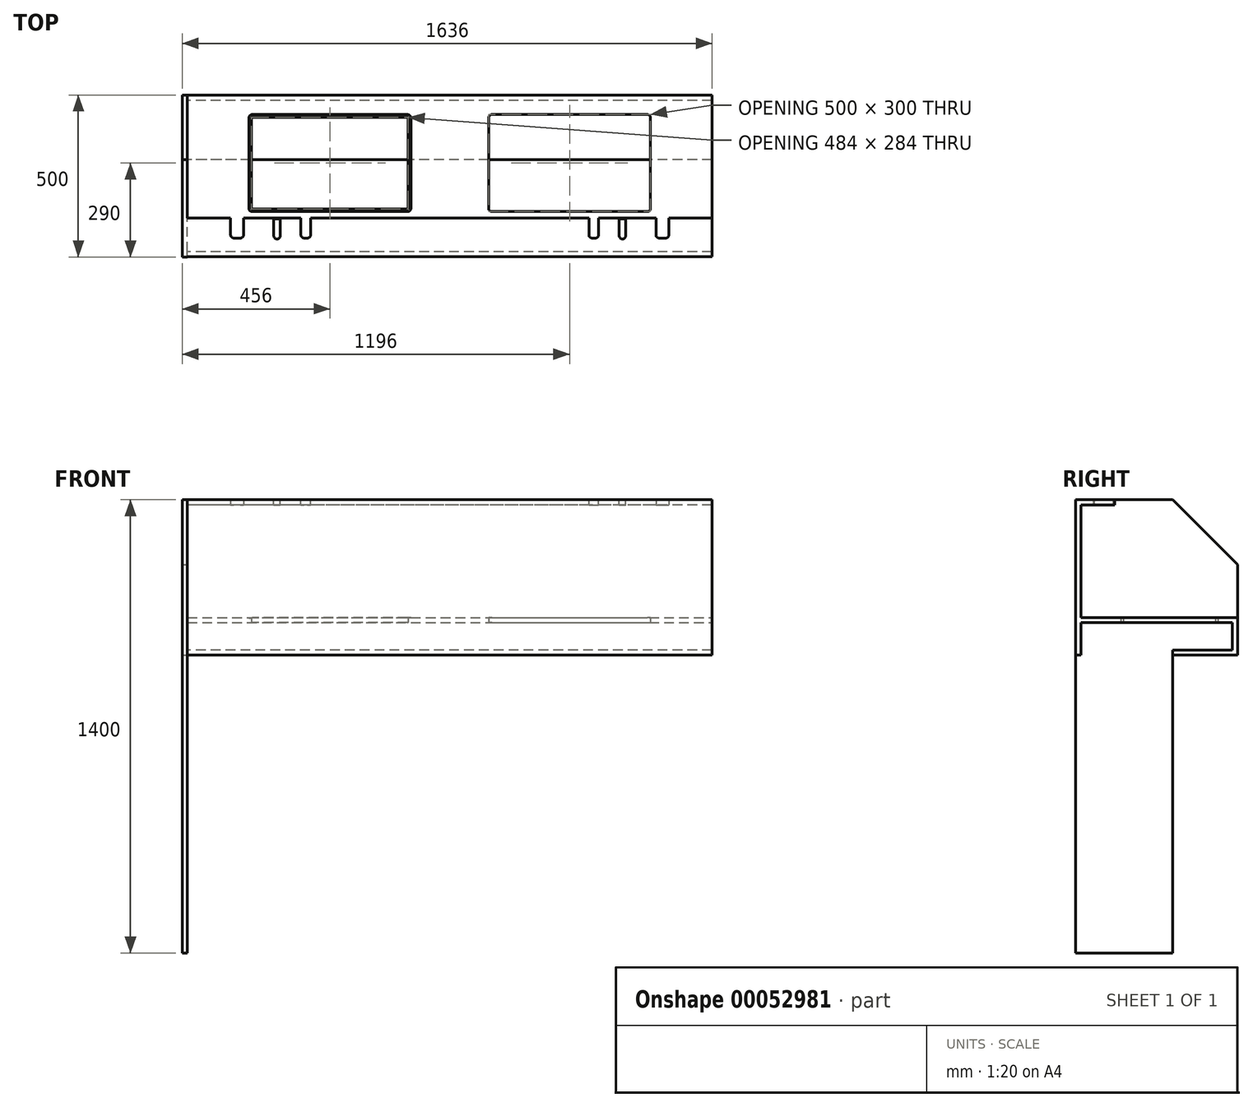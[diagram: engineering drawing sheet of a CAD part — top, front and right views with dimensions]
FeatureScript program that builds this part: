
annotation { "Feature Type Name" : "Feature", "Feature Type Description" : "" }
export const myFeature = defineFeature(function(context is Context, id is Id, definition is map)
    precondition{}
    {
        {
            var Q0;
            Q0=qCreatedBy(makeId("Right.planeOp"),FACE);
            var sketch = newSketch(context, id + "F0", { "sketchPlane" : qUnion([Q0])});
            skLineSegment(sketch, "E0", {"start": v(-300, 480) * mm, "end": v(-300, -920) * mm});
            skLineSegment(sketch, "E1", {"start": v(0, -920) * mm, "end": v(-300, -920) * mm});
            skLineSegment(sketch, "E2", {"start": v(200, 0) * mm, "end": v(200, 280) * mm});
            skLineSegment(sketch, "E3", {"start": v(200, 280) * mm, "end": v(0, 480) * mm});
            skLineSegment(sketch, "E4", {"start": v(0, 480) * mm, "end": v(-300, 480) * mm});
            skLineSegment(sketch, "E5", {"start": v(0, 647.9) * mm, "end": v(0, -1632.93) * mm, "construction": true});
            skLineSegment(sketch, "E6", {"start": v(-901.91, 0) * mm, "end": v(413.04, 0) * mm, "construction": true});
            skLineSegment(sketch, "E7", {"start": v(0, -920) * mm, "end": v(0, 0) * mm});
            skLineSegment(sketch, "E8", {"start": v(0, 0) * mm, "end": v(200, 0) * mm});
            skPoint(sketch, "E9.orphan", {"position": v(1728, 0) * mm});
            skSolve(sketch);
        }
        {
            var Q0;
            Q0=makeQuery(id+"F0.imprint","IMPRINT",FACE,{"disambiguationData":[TD([[makeQuery(id+"F0.imprint","IMPRINT",EDGE,{"derivedFrom":sQuery(id+"F0.wireOp",EDGE,"E0")}),1.0]])]});
            var Q1;
            Q1 = qSketchRegion(id + "F3", true);
            extrude(context, id + "F1", {"entities" : qUnion([Q0, Q1]), "oppositeDirection" : true, "depth" : 16 * mm});
        }
        {
            var Q0;
            Q0=qCreatedBy(makeId("Top.planeOp"),FACE);
            cPlane(context, id + "F2", {"entities" : qUnion([Q0]), "cplaneType" : CPlaneType.OFFSET, "offset" : 100 * mm, "width" : 150 * mm, "height" : 150 * mm});
        }
        {
            var Q0;
            Q0=qCreatedBy(id+"F2.planeOp",FACE);
            var sketch = newSketch(context, id + "F3", { "sketchPlane" : qUnion([Q0])});
            skLineSegment(sketch, "E10.bottom", {"start": v(0, -284) * mm, "end": v(1620, -284) * mm});
            skLineSegment(sketch, "E10.top", {"start": v(0, 200) * mm, "end": v(1620, 200) * mm});
            skLineSegment(sketch, "E10.left", {"start": v(0, -284) * mm, "end": v(0, 200) * mm});
            skLineSegment(sketch, "E10.right", {"start": v(1620, -284) * mm, "end": v(1620, 200) * mm});
            skLineSegment(sketch, "E11", {"start": v(0, 0) * mm, "end": v(1326.37, 0) * mm, "construction": true});
            skLineSegment(sketch, "E12", {"start": v(810, -795.49) * mm, "end": v(810, 1180.36) * mm, "construction": true});
            skPoint(sketch, "E12.endSnap0", {"position": v(810, 200) * mm});
            skLineSegment(sketch, "E13.top", {"start": v(680, 140) * mm, "end": v(200, 140) * mm});
            skLineSegment(sketch, "E13.left", {"start": v(690, -150) * mm, "end": v(690, 130) * mm});
            skLineSegment(sketch, "E13.right", {"start": v(190, -150) * mm, "end": v(190, 130) * mm});
            skLineSegment(sketch, "E14", {"start": v(680, -160) * mm, "end": v(200, -160) * mm});
            skPoint(sketch, "E15.visualSharp", {"position": v(690, -160) * mm});
            skArc(sketch, "E15.filletArc", {"start": v(680, -160) * mm, "mid": v(687.07, -157.07) * mm, "end": v(690, -150) * mm});
            skPoint(sketch, "E16.visualSharp", {"position": v(190, -160) * mm});
            skArc(sketch, "E16.filletArc", {"start": v(190, -150) * mm, "mid": v(192.93, -157.07) * mm, "end": v(200, -160) * mm});
            skPoint(sketch, "E17.visualSharp", {"position": v(190, 140) * mm});
            skArc(sketch, "E17.filletArc", {"start": v(200, 140) * mm, "mid": v(192.93, 137.07) * mm, "end": v(190, 130) * mm});
            skPoint(sketch, "E18.visualSharp", {"position": v(690, 140) * mm});
            skArc(sketch, "E18.filletArc", {"start": v(690, 130) * mm, "mid": v(687.07, 137.07) * mm, "end": v(680, 140) * mm});
            skArc(sketch, "E19.0", {"start": v(680, -152) * mm, "mid": v(681.41, -151.41) * mm, "end": v(682, -150) * mm});
            skLineSegment(sketch, "E19.1", {"start": v(682, -150) * mm, "end": v(682, 130) * mm});
            skLineSegment(sketch, "E19.2", {"start": v(680, -152) * mm, "end": v(200, -152) * mm});
            skArc(sketch, "E19.3", {"start": v(682, 130) * mm, "mid": v(681.41, 131.41) * mm, "end": v(680, 132) * mm});
            skArc(sketch, "E19.4", {"start": v(198, -150) * mm, "mid": v(198.59, -151.41) * mm, "end": v(200, -152) * mm});
            skLineSegment(sketch, "E19.5", {"start": v(198, -150) * mm, "end": v(198, 130) * mm});
            skArc(sketch, "E19.6", {"start": v(200, 132) * mm, "mid": v(198.59, 131.41) * mm, "end": v(198, 130) * mm});
            skLineSegment(sketch, "E19.7", {"start": v(680, 132) * mm, "end": v(200, 132) * mm});
            skArc(sketch, "E20.MirrorCS", {"start": v(1420, 140) * mm, "mid": v(1427.07, 137.07) * mm, "end": v(1430, 130) * mm});
            skArc(sketch, "E21.MirrorCS", {"start": v(1420, 132) * mm, "mid": v(1421.41, 131.41) * mm, "end": v(1422, 130) * mm});
            skArc(sketch, "E22.MirrorCS", {"start": v(1422, -150) * mm, "mid": v(1421.41, -151.41) * mm, "end": v(1420, -152) * mm});
            skArc(sketch, "E23.MirrorCS", {"start": v(930, 130) * mm, "mid": v(932.93, 137.07) * mm, "end": v(940, 140) * mm});
            skArc(sketch, "E24.MirrorCS", {"start": v(940, -152) * mm, "mid": v(938.59, -151.41) * mm, "end": v(938, -150) * mm});
            skArc(sketch, "E25.MirrorCS", {"start": v(940, -160) * mm, "mid": v(932.93, -157.07) * mm, "end": v(930, -150) * mm});
            skArc(sketch, "E26.MirrorCS", {"start": v(1430, -150) * mm, "mid": v(1427.07, -157.07) * mm, "end": v(1420, -160) * mm});
            skLineSegment(sketch, "E27.MirrorCS", {"start": v(938, -150) * mm, "end": v(938, 130) * mm});
            skLineSegment(sketch, "E28.MirrorCS", {"start": v(1430, -150) * mm, "end": v(1430, 130) * mm});
            skPoint(sketch, "E29.MirrorP", {"position": v(930, 140) * mm});
            skLineSegment(sketch, "E30.MirrorCS", {"start": v(930, -150) * mm, "end": v(930, 130) * mm});
            skLineSegment(sketch, "E31.MirrorCS", {"start": v(940, -152) * mm, "end": v(1420, -152) * mm});
            skLineSegment(sketch, "E32.MirrorCS", {"start": v(940, 140) * mm, "end": v(1420, 140) * mm});
            skPoint(sketch, "E33.MirrorP", {"position": v(1430, 140) * mm});
            skLineSegment(sketch, "E34.MirrorCS", {"start": v(940, 132) * mm, "end": v(1420, 132) * mm});
            skLineSegment(sketch, "E35.MirrorCS", {"start": v(1422, -150) * mm, "end": v(1422, 130) * mm});
            skLineSegment(sketch, "E36.MirrorCS", {"start": v(940, -160) * mm, "end": v(1420, -160) * mm});
            skPoint(sketch, "E37.MirrorP", {"position": v(1430, -160) * mm});
            skPoint(sketch, "E38.MirrorP", {"position": v(930, -160) * mm});
            skSolve(sketch);
        }
        {
            var Q0;
            Q0=makeQuery(id+"F3.imprint","IMPRINT",FACE,{"disambiguationData":[TD([[makeQuery(id+"F3.imprint","IMPRINT",EDGE,{"derivedFrom":sQuery(id+"F3.wireOp",EDGE,"E10.bottom")}),1.0]])]});
            extrude(context, id + "F4", {"entities" : qUnion([Q0]), "operationType" : NewBodyOperationType.ADD, "depth" : 16 * mm});
        }
        {
            var Q0;
            Q0=makeQuery(id+"F3.imprint","IMPRINT",FACE,{"disambiguationData":[TD([[makeQuery(id+"F3.imprint","IMPRINT",EDGE,{"derivedFrom":sQuery(id+"F3.wireOp",EDGE,"E13.top")}),1.0]])]});
            var Q1;
            Q1=makeQuery(id+"F3.imprint","IMPRINT",FACE,{"disambiguationData":[TD([[makeQuery(id+"F3.imprint","IMPRINT",EDGE,{"derivedFrom":sQuery(id+"F3.wireOp",EDGE,"E20.MirrorCS")}),-1.0]])]});
            extrude(context, id + "F5", {"entities" : qUnion([Q0, Q1]), "operationType" : NewBodyOperationType.ADD, "depth" : 14 * mm});
        }
        {
            var Q0;
            Q0=makeQuery(id+"F0.imprint","IMPRINT",FACE,{"disambiguationData":[TD([[makeQuery(id+"F0.imprint","IMPRINT",EDGE,{"derivedFrom":sQuery(id+"F0.wireOp",EDGE,"E0")}),1.0]])]});
            var sketch = newSketch(context, id + "F6", { "sketchPlane" : qUnion([Q0])});
            skLineSegment(sketch, "E39.bottom", {"start": v(0, 0) * mm, "end": v(0, 0) * mm});
            skLineSegment(sketch, "E40.bottom", {"start": v(184, 16) * mm, "end": v(0, 16) * mm});
            skLineSegment(sketch, "E40.top", {"start": v(184, 0) * mm, "end": v(0, 0) * mm});
            skLineSegment(sketch, "E40.left", {"start": v(184, 16) * mm, "end": v(184, 0) * mm});
            skLineSegment(sketch, "E41", {"start": v(0, 16) * mm, "end": v(0, 0) * mm});
            skLineSegment(sketch, "E42.bottom", {"start": v(184, 0) * mm, "end": v(200, 0) * mm});
            skLineSegment(sketch, "E42.top", {"start": v(184, 100) * mm, "end": v(200, 100) * mm});
            skLineSegment(sketch, "E42.left", {"start": v(184, 0) * mm, "end": v(184, 100) * mm});
            skLineSegment(sketch, "E42.right", {"start": v(200, 0) * mm, "end": v(200, 100) * mm});
            skLineSegment(sketch, "E43.bottom", {"start": v(-299.51, 0) * mm, "end": v(-283.51, 0) * mm});
            skLineSegment(sketch, "E43.top", {"start": v(-299.51, 464) * mm, "end": v(-283.51, 464) * mm});
            skLineSegment(sketch, "E43.left", {"start": v(-299.51, 0) * mm, "end": v(-299.51, 464) * mm});
            skLineSegment(sketch, "E43.right", {"start": v(-283.51, 0) * mm, "end": v(-283.51, 464) * mm});
            skLineSegment(sketch, "E44.bottom", {"start": v(-299.51, 464) * mm, "end": v(-179.51, 464) * mm});
            skLineSegment(sketch, "E44.top", {"start": v(-299.51, 480) * mm, "end": v(-179.51, 480) * mm});
            skLineSegment(sketch, "E44.left", {"start": v(-299.51, 464) * mm, "end": v(-299.51, 480) * mm});
            skLineSegment(sketch, "E44.right", {"start": v(-179.51, 464) * mm, "end": v(-179.51, 480) * mm});
            skSolve(sketch);
        }
        {
            var Q0;
            Q0 = qSketchRegion(id + "F6", true);
            extrude(context, id + "F7", {"entities" : qUnion([Q0]), "operationType" : NewBodyOperationType.ADD, "depth" : 1620 * mm});
        }
        {
            var Q0;
            Q0=makeQuery(id+"F7.boolean.opBoolean","MERGE",FACE,{"derivedFrom":[makeQuery(id+"F1.opExtrude","SWEPT_FACE",FACE,{"disambiguationData":[OSD([sQuery(id+"F0.wireOp",EDGE,"E4")])]}),makeQuery(id+"F7.opExtrude","SWEPT_FACE",FACE,{"disambiguationData":[OSD([sQuery(id+"F6.wireOp",EDGE,"E43.top"),sQuery(id+"F6.wireOp",EDGE,"E44.top")])]})]});
            var sketch = newSketch(context, id + "F8", { "sketchPlane" : qUnion([Q0])});
            skLineSegment(sketch, "E45.bottom", {"start": v(276.69, -244.46) * mm, "end": v(276.69, -244.46) * mm});
            skLineSegment(sketch, "E45.top", {"start": v(266.69, -182.58) * mm, "end": v(286.69, -182.58) * mm});
            skLineSegment(sketch, "E45.left", {"start": v(266.69, -234.46) * mm, "end": v(266.69, -182.58) * mm});
            skLineSegment(sketch, "E45.right", {"start": v(286.69, -234.46) * mm, "end": v(286.69, -182.58) * mm});
            skLineSegment(sketch, "E46.bottom", {"start": v(370.4, -241.58) * mm, "end": v(360.4, -241.58) * mm});
            skLineSegment(sketch, "E46.top", {"start": v(380.4, -171.06) * mm, "end": v(350.4, -171.06) * mm});
            skLineSegment(sketch, "E46.left", {"start": v(380.4, -231.58) * mm, "end": v(380.4, -171.06) * mm});
            skLineSegment(sketch, "E46.right", {"start": v(350.4, -231.58) * mm, "end": v(350.4, -171.06) * mm});
            skLineSegment(sketch, "E47.bottom", {"start": v(173.36, -174.4) * mm, "end": v(133.36, -174.4) * mm});
            skLineSegment(sketch, "E47.top", {"start": v(163.36, -241.58) * mm, "end": v(143.36, -241.58) * mm});
            skLineSegment(sketch, "E47.left", {"start": v(173.36, -174.4) * mm, "end": v(173.36, -231.58) * mm});
            skLineSegment(sketch, "E47.right", {"start": v(133.36, -174.4) * mm, "end": v(133.36, -231.58) * mm});
            skPoint(sketch, "E48.visualSharp", {"position": v(133.36, -241.58) * mm});
            skArc(sketch, "E48.filletArc", {"start": v(133.36, -231.58) * mm, "mid": v(136.3, -238.65) * mm, "end": v(143.36, -241.58) * mm});
            skPoint(sketch, "E49.visualSharp", {"position": v(173.36, -241.58) * mm});
            skArc(sketch, "E49.filletArc", {"start": v(163.36, -241.58) * mm, "mid": v(170.44, -238.65) * mm, "end": v(173.36, -231.58) * mm});
            skPoint(sketch, "E50.visualSharp", {"position": v(266.69, -244.46) * mm});
            skArc(sketch, "E50.filletArc", {"start": v(266.69, -234.46) * mm, "mid": v(269.62, -241.53) * mm, "end": v(276.69, -244.46) * mm});
            skPoint(sketch, "E51.visualSharp", {"position": v(286.69, -244.46) * mm});
            skArc(sketch, "E51.filletArc", {"start": v(276.69, -244.46) * mm, "mid": v(283.76, -241.53) * mm, "end": v(286.69, -234.46) * mm});
            skPoint(sketch, "E52.visualSharp", {"position": v(350.4, -241.58) * mm});
            skArc(sketch, "E52.filletArc", {"start": v(350.4, -231.58) * mm, "mid": v(353.33, -238.65) * mm, "end": v(360.4, -241.58) * mm});
            skPoint(sketch, "E53.visualSharp", {"position": v(380.4, -241.58) * mm});
            skArc(sketch, "E53.filletArc", {"start": v(370.4, -241.58) * mm, "mid": v(377.47, -238.65) * mm, "end": v(380.4, -231.58) * mm});
            skLineSegment(sketch, "E54.MirrorCS", {"start": v(1249.6, -241.58) * mm, "end": v(1259.6, -241.58) * mm});
            skArc(sketch, "E55.MirrorCS", {"start": v(1353.31, -234.46) * mm, "mid": v(1350.38, -241.53) * mm, "end": v(1343.31, -244.46) * mm});
            skArc(sketch, "E56.MirrorCS", {"start": v(1343.31, -244.46) * mm, "mid": v(1336.24, -241.53) * mm, "end": v(1333.31, -234.46) * mm});
            skArc(sketch, "E57.MirrorCS", {"start": v(1269.6, -231.58) * mm, "mid": v(1266.67, -238.65) * mm, "end": v(1259.6, -241.58) * mm});
            skArc(sketch, "E58.MirrorCS", {"start": v(1456.64, -241.58) * mm, "mid": v(1449.56, -238.65) * mm, "end": v(1446.64, -231.58) * mm});
            skArc(sketch, "E59.MirrorCS", {"start": v(1249.6, -241.58) * mm, "mid": v(1242.53, -238.65) * mm, "end": v(1239.6, -231.58) * mm});
            skLineSegment(sketch, "E60.MirrorCS", {"start": v(1456.64, -241.58) * mm, "end": v(1476.64, -241.58) * mm});
            skPoint(sketch, "E61.MirrorP", {"position": v(1353.31, -244.46) * mm});
            skPoint(sketch, "E62.MirrorP", {"position": v(1269.6, -241.58) * mm});
            skPoint(sketch, "E63.MirrorP", {"position": v(1446.64, -241.58) * mm});
            skPoint(sketch, "E64.MirrorP", {"position": v(1239.6, -241.58) * mm});
            skPoint(sketch, "E65.MirrorP", {"position": v(1333.31, -244.46) * mm});
            skLineSegment(sketch, "E66.MirrorCS", {"start": v(1343.31, -244.46) * mm, "end": v(1343.31, -244.46) * mm});
            skLineSegment(sketch, "E67.MirrorCS", {"start": v(1353.31, -182.58) * mm, "end": v(1333.31, -182.58) * mm});
            skLineSegment(sketch, "E68.MirrorCS", {"start": v(1486.64, -174.4) * mm, "end": v(1486.64, -231.58) * mm});
            skLineSegment(sketch, "E69.MirrorCS", {"start": v(1353.31, -234.46) * mm, "end": v(1353.31, -182.58) * mm});
            skLineSegment(sketch, "E70.MirrorCS", {"start": v(1333.31, -234.46) * mm, "end": v(1333.31, -182.58) * mm});
            skLineSegment(sketch, "E71.MirrorCS", {"start": v(1239.6, -171.06) * mm, "end": v(1269.6, -171.06) * mm});
            skLineSegment(sketch, "E72.MirrorCS", {"start": v(1239.6, -231.58) * mm, "end": v(1239.6, -171.06) * mm});
            skLineSegment(sketch, "E73.MirrorCS", {"start": v(1446.64, -174.4) * mm, "end": v(1446.64, -231.58) * mm});
            skLineSegment(sketch, "E74.MirrorCS", {"start": v(1269.6, -231.58) * mm, "end": v(1269.6, -171.06) * mm});
            skLineSegment(sketch, "E75.MirrorCS", {"start": v(1446.64, -174.4) * mm, "end": v(1486.64, -174.4) * mm});
            skArc(sketch, "E76.MirrorCS", {"start": v(1486.64, -231.58) * mm, "mid": v(1483.7, -238.65) * mm, "end": v(1476.64, -241.58) * mm});
            skSolve(sketch);
        }
        {
            var Q0;
            Q0 = qSketchRegion(id + "F8", true);
            extrude(context, id + "F9", {"entities" : qUnion([Q0]), "operationType" : NewBodyOperationType.REMOVE, "oppositeDirection" : true, "depth" : 25 * mm});
        }
    });
